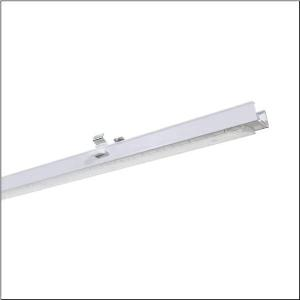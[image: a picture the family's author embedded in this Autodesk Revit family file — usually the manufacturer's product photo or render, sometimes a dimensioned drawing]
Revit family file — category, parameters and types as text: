
# Revit family: trunking_flex_31_51re12ma66b
name_source: partatom
category: Lighting Fixtures
units: mm (PartAtom-declared; Revit-internal decimal feet)

## family parameters
Cut with Voids When Loaded = No
Host = Face
Light Source = No
Part Type = Normal
Room Calculation Point = No
Round Connector Dimension = Use Diameter
Shared = No

## types (1)
- --- (1 x LED, 6400 lm, 40 W, 6500K)
    Apparent Load = 40 VA
    CIE Flux Codes = 65 91 98 99 100
    Color Rendering = 80
    Color Temperature = 6500K
    Default Elevation = 1800 mm
    Description = Trunking Flex 31, luminaire insert, of extruded aluminium section, coated, traffic white (RAL 9016), length: 1.172mm, width: 91mm, height: 53mm, LED rated luminous flux: 6.400lm, light colour: 865, control gear: ON/OFF Multilumen, with system connector: socket, mains connection: 220..240V, AC, 50/60Hz, rated input power: 40W, luminous flux adjustable on luminaire in four steps (3420/4540/5580/6630lm), connected load according to luminous flux setting (20/26/33/40W), primary light control with lens, of plastic, primary optical cover: cover, of PMMA, light emission: direct distribution, protection rating (complete): IP20, insulation class (complete): insulation class I (protective earthing), certification: CE, UKCA, impact resistance: IK02, permissible ambient temperature for indoor applications: -20..+40°C, packaging unit: 1 piece
    Height = 58 mm
    Lamp = 1 x LED
    Lamp Light Flux = 6400 lm
    Lamp Power = 40 W
    Lamp count = 1
    Length = 1172 mm
    Luminous efficacy = 160 lm/W
    Manufacturer = Siteco
    ModVariant = No
    Model = 51RE12MA66B
    Mounting Place = Ceiling
    Mounting Type = Pendant
    Number of Poles = 1
    OnlyDefault = Yes
    Power Factor = 1
    Product Name = Trunking Flex 31
    Product group = luminaire insert
    ProductGroupID = 901
    Protection Class = Protection class I
    Protection Degree = IP 20
    RLX_Detail_Level = 1
    RLX_Emergency_Light_Flux = 0 lm
    RLX_Emergency_Type = 0
    RLX_Emergency_Type_DB = No
    RlxData = <blob elided: 19921 chars, md5=f9135cff>
    Socket = socket
    Standby Power = 0 W
    System Light Flux = 6400 lm
    System Power = 40 W
    Type Comments = factory setting: luminous flux: 100 % | (ON | ON) | 300 mA
    Type Image = l_1266702.jpg
    URL = http://relux.com
    VarID = @adj_001289
    Voltage = 0 V
    Weight = 0.00 kg
    Width = 65 mm

## geometry (parser evidence)
native form markers: Blend x4, Sweep x9
no freeform markers — native parametric forms only
